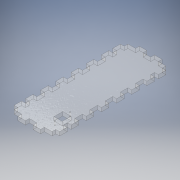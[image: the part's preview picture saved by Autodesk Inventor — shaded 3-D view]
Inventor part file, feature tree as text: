
AUTODESK INVENTOR PART (.ipt)
format: ipt  version: 2019 (Build 230136000, 136)  size: 226,304 bytes
history: native  units: mm
features: extrude x1, sketch x1
ambient origin geometry x8: Origin, YZ Plane, XZ Plane, XY Plane, X Axis, Y Axis, Z Axis, Center Point
bodies: Solid1 (feature_tree)
feature tree (2):
  extrude  "Extrusion1"  Depth=180.0mm
  sketch  "Sketch1"  dims[d0=60.0mm d1=180.0mm d2=6.0mm d3=6.0mm d4=12.0mm d5=12.0mm d6=12.0mm d7=12.0mm d8=12.0mm d9=6.0mm d10=12.0mm d15=6.0mm d16=0.0mm d17=6.0mm d19=6.0mm d20=12.0mm d24=6.0mm d25=13.0mm d26=14.0mm d27=22.0mm d28=1.8mm d30=5.0mm d31=5.0mm]
